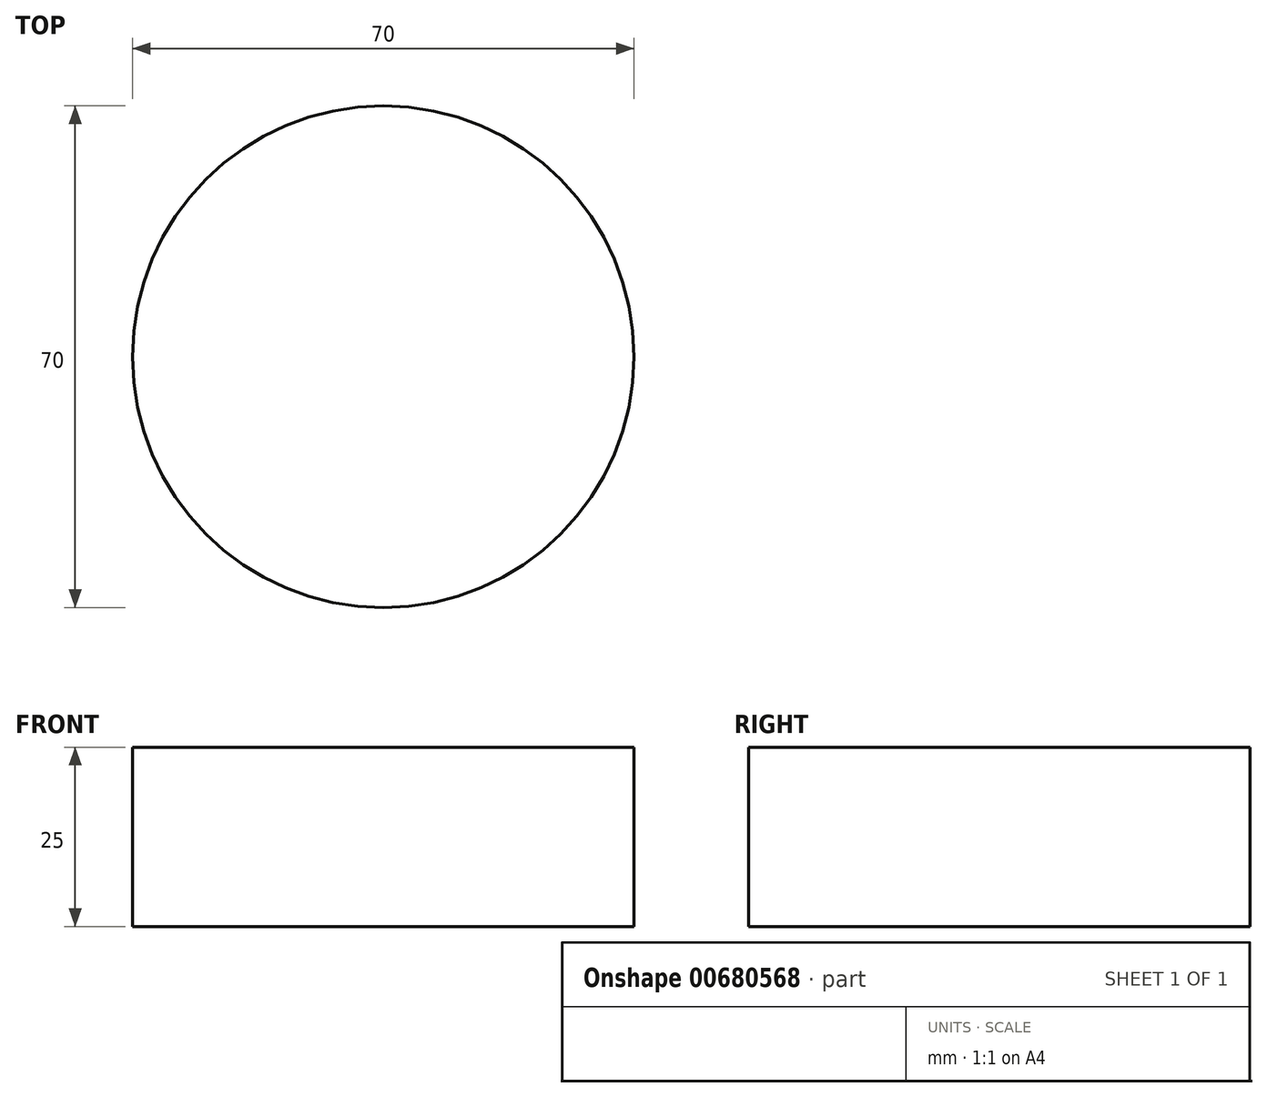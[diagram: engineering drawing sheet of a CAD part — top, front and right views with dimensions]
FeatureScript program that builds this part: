
annotation { "Feature Type Name" : "Feature", "Feature Type Description" : "" }
export const myFeature = defineFeature(function(context is Context, id is Id, definition is map)
    precondition{}
    {
        {
            var Q0;
            Q0=qCreatedBy(makeId("Right.planeOp"),FACE);
            var sketch = newSketch(context, id + "F0", { "sketchPlane" : qUnion([Q0])});
            skPoint(sketch, "E0.middle", {"position": v(0, 0) * mm});
            skLineSegment(sketch, "E1.bottom", {"start": v(0, 25) * mm, "end": v(35, 25) * mm});
            skLineSegment(sketch, "E1.top", {"start": v(0, 0) * mm, "end": v(35, 0) * mm});
            skLineSegment(sketch, "E1.left", {"start": v(0, 25) * mm, "end": v(0, 0) * mm});
            skLineSegment(sketch, "E1.right", {"start": v(35, 25) * mm, "end": v(35, 0) * mm});
            skLineSegment(sketch, "E2", {"start": v(0, 45.59) * mm, "end": v(0, -9.56) * mm});
            skSolve(sketch);
        }
        {
            var Q0;
            {var subQ0=sQuery(id+"F0.wireOp",EDGE,"E1.bottom");Q0=makeQuery(id+"F0.imprint","IMPRINT",FACE,{"disambiguationData":[TD([[makeQuery(id+"F0.imprint","IMPRINT",EDGE,{"derivedFrom":subQ0}),-1.0]])]});}
            var Q1;
            Q1=sQuery(id+"F0.wireOp",EDGE,"E2");
            revolve(context, id + "F1", {"entities" : qUnion([Q0]), "axis" : qUnion([Q1]), "revolveType" : RevolveType.FULL, "surfaceOperationType" : NewSurfaceOperationType.NEW});
        }
    });
